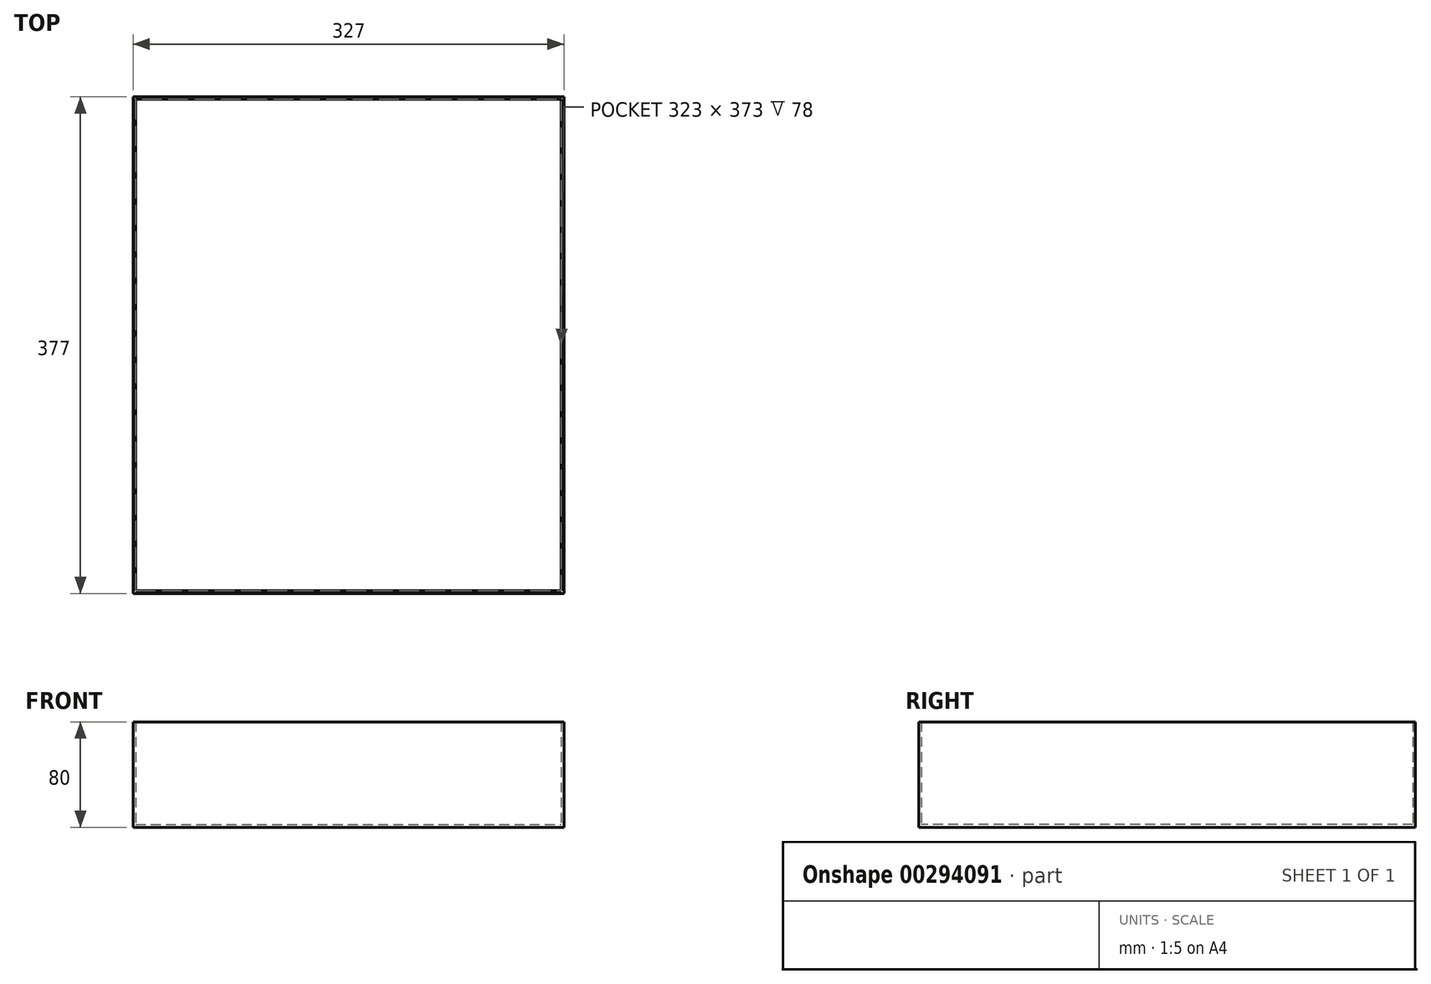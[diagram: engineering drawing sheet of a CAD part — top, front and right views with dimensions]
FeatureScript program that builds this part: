
annotation { "Feature Type Name" : "Feature", "Feature Type Description" : "" }
export const myFeature = defineFeature(function(context is Context, id is Id, definition is map)
    precondition{}
    {
        {
            assignVariable(context, id + "F0", {"name" : "BoxHeight", "anyValue" : 80 * mm});
        }
        {
            var Q0;
            Q0=qCreatedBy(makeId("Top.planeOp"),FACE);
            var sketch = newSketch(context, id + "F1", { "sketchPlane" : qUnion([Q0])});
            skLineSegment(sketch, "E0.bottom", {"start": v(-163.5, 188.5) * mm, "end": v(163.5, 188.5) * mm});
            skLineSegment(sketch, "E0.top", {"start": v(-163.5, -188.5) * mm, "end": v(163.5, -188.5) * mm});
            skLineSegment(sketch, "E0.left", {"start": v(-163.5, 188.5) * mm, "end": v(-163.5, -188.5) * mm});
            skLineSegment(sketch, "E0.right", {"start": v(163.5, 188.5) * mm, "end": v(163.5, -188.5) * mm});
            skPoint(sketch, "E0.middle", {"position": v(0, 0) * mm});
            skLineSegment(sketch, "E1.0", {"start": v(-161.5, 186.5) * mm, "end": v(161.5, 186.5) * mm});
            skLineSegment(sketch, "E1.1", {"start": v(-161.5, 186.5) * mm, "end": v(-161.5, -186.5) * mm});
            skLineSegment(sketch, "E1.2", {"start": v(-161.5, -186.5) * mm, "end": v(161.5, -186.5) * mm});
            skLineSegment(sketch, "E1.3", {"start": v(161.5, 186.5) * mm, "end": v(161.5, -186.5) * mm});
            skSolve(sketch);
        }
        {
            var Q0;
            Q0=makeQuery(id+"F1.imprint","IMPRINT",FACE,{"disambiguationData":[TD([[makeQuery(id+"F1.imprint","IMPRINT",EDGE,{"derivedFrom":sQuery(id+"F1.wireOp",EDGE,"E0.bottom")}),-1.0]])]});
            extrude(context, id + "F2", {"entities" : qUnion([Q0]), "depth" : getVariable(context, 'BoxHeight')});
        }
        {
            var Q0;
            Q0 = qSketchRegion(id + "F1", true);
            var Q1;
            Q1=makeQuery(id+"F1.imprint","IMPRINT",FACE,{"disambiguationData":[TD([[makeQuery(id+"F1.imprint","IMPRINT",EDGE,{"derivedFrom":sQuery(id+"F1.wireOp",EDGE,"E1.0")}),-1.0]])]});
            extrude(context, id + "F3", {"entities" : qUnion([Q0, Q1]), "operationType" : NewBodyOperationType.ADD, "depth" : 2 * mm});
        }
        {
            var Q0;
            Q0=makeQuery(id+"F2.opExtrude","SWEPT_FACE",FACE,{"disambiguationData":[OSD([sQuery(id+"F1.wireOp",EDGE,"E0.top")])]});
            var sketch = newSketch(context, id + "F4", { "sketchPlane" : qUnion([Q0])});
            skLineSegment(sketch, "E2", {"start": v(0, 80) * mm, "end": v(0, 0) * mm, "construction": true});
            skLineSegment(sketch, "E3", {"start": v(0, 40) * mm, "end": v(-50, 40) * mm, "construction": true});
            skLineSegment(sketch, "E4.MirrorCS", {"start": v(0, 40) * mm, "end": v(50, 40) * mm, "construction": true});
            skCircle(sketch, "E5", {"center": v(-50, 40) * mm, "radius": 2.5 * mm});
            skSolve(sketch);
        }
        {
            var Q0;
            Q0=sQuery(id+"F4.wireOp",EDGE,"E3");
            cPlane(context, id + "F5", {"entities" : qUnion([Q0]), "cplaneType" : CPlaneType.LINE_ANGLE, "offset" : 25 * mm, "angle" : 90 * degree, "width" : 150 * mm, "height" : 150 * mm});
        }
    });
